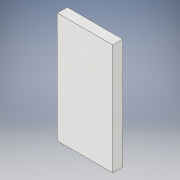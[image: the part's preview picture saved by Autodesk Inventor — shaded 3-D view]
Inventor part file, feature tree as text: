
AUTODESK INVENTOR PART (.ipt)
format: ipt  version: 2019 (Build 230136000, 136)  size: 103,936 bytes
history: native  units: in
note: dims shown in document units (in); Inventor stores cm internally (conversion verified against a paired STEP export)
features: extrude x1, sketch x1
ambient origin geometry x8: Origin, YZ Plane, XZ Plane, XY Plane, X Axis, Y Axis, Z Axis, Center Point
bodies: Solid1 (feature_tree)
feature tree (2):
  extrude  "Extrusion1"  Depth=0.1181in
  sketch  "Sketch1"  dims[d0=0.6496in d1=0.1181in d2=1.2992in d3=0.0in]
